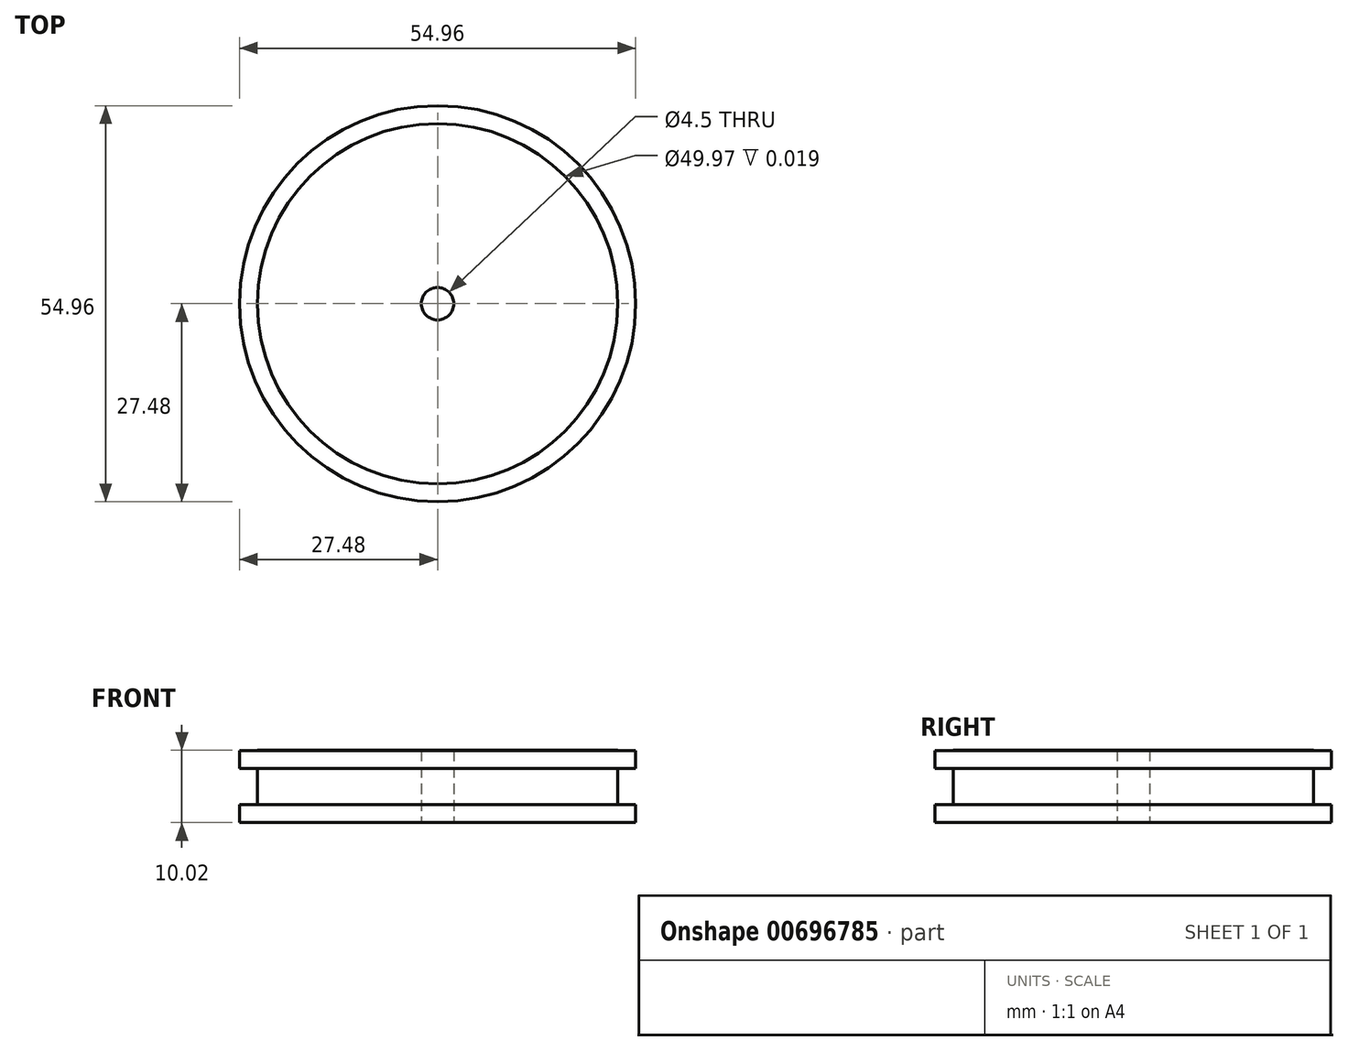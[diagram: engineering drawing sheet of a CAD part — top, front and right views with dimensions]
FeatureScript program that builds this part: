
annotation { "Feature Type Name" : "Feature", "Feature Type Description" : "" }
export const myFeature = defineFeature(function(context is Context, id is Id, definition is map)
    precondition{}
    {
        {
            var Q0;
            Q0=qCreatedBy(makeId("Top.planeOp"),FACE);
            var sketch = newSketch(context, id + "F0", { "sketchPlane" : qUnion([Q0])});
            skCircle(sketch, "E0", {"center": v(0, 0) * mm, "radius": 25 * mm});
            skCircle(sketch, "E1", {"center": v(0, 0) * mm, "radius": 2.25 * mm});
            skSolve(sketch);
        }
        {
            var Q0;
            Q0=makeQuery(id+"F0.imprint","IMPRINT",FACE,{"disambiguationData":[TD([[makeQuery(id+"F0.imprint","IMPRINT",EDGE,{"derivedFrom":sQuery(id+"F0.wireOp",EDGE,"E0")}),1.0]])]});
            extrude(context, id + "F1", {"entities" : qUnion([Q0]), "endBound" : BoundingType.SYMMETRIC, "depth" : 10 * mm, "offsetDistance" : 25 * mm});
        }
        {
            var Q0;
            Q0=qCreatedBy(makeId("Right.planeOp"),FACE);
            var sketch = newSketch(context, id + "F2", { "sketchPlane" : qUnion([Q0])});
            skLineSegment(sketch, "E2", {"start": v(24.98, 4.98) * mm, "end": v(24.98, -5.02) * mm});
            skLineSegment(sketch, "E3.bottom", {"start": v(24.98, 4.98) * mm, "end": v(27.48, 4.98) * mm});
            skLineSegment(sketch, "E3.top", {"start": v(24.98, 2.48) * mm, "end": v(27.48, 2.48) * mm});
            skLineSegment(sketch, "E3.left", {"start": v(24.98, 4.98) * mm, "end": v(24.98, 2.48) * mm});
            skLineSegment(sketch, "E3.right", {"start": v(27.48, 4.98) * mm, "end": v(27.48, 2.48) * mm});
            skLineSegment(sketch, "E4.bottom", {"start": v(24.98, -5.02) * mm, "end": v(27.48, -5.02) * mm});
            skLineSegment(sketch, "E4.top", {"start": v(24.98, -2.52) * mm, "end": v(27.48, -2.52) * mm});
            skLineSegment(sketch, "E4.left", {"start": v(24.98, -5.02) * mm, "end": v(24.98, -2.52) * mm});
            skLineSegment(sketch, "E4.right", {"start": v(27.48, -5.02) * mm, "end": v(27.48, -2.52) * mm});
            skSolve(sketch);
        }
        {
            var Q0;
            Q0=makeQuery(id+"F2.imprint","IMPRINT",FACE,{"disambiguationData":[TD([[makeQuery(id+"F2.imprint","IMPRINT",EDGE,{"derivedFrom":sQuery(id+"F2.wireOp",EDGE,"E3.bottom")}),-1.0]])]});
            var Q1;
            Q1=makeQuery(id+"F2.imprint","IMPRINT",FACE,{"disambiguationData":[TD([[makeQuery(id+"F2.imprint","IMPRINT",EDGE,{"derivedFrom":sQuery(id+"F2.wireOp",EDGE,"E4.bottom")}),1.0]])]});
            var Q2;
            Q2=makeQuery(id+"F1.opExtrude","CAP_EDGE",EDGE,{"disambiguationData":[OSD([sQuery(id+"F0.wireOp",EDGE,"E1")])],"isStart":false});
            revolve(context, id + "F3", {"operationType" : NewBodyOperationType.ADD, "entities" : qUnion([Q0, Q1]), "axis" : qUnion([Q2]), "revolveType" : RevolveType.FULL, "surfaceOperationType" : NewSurfaceOperationType.NEW});
        }
    });
